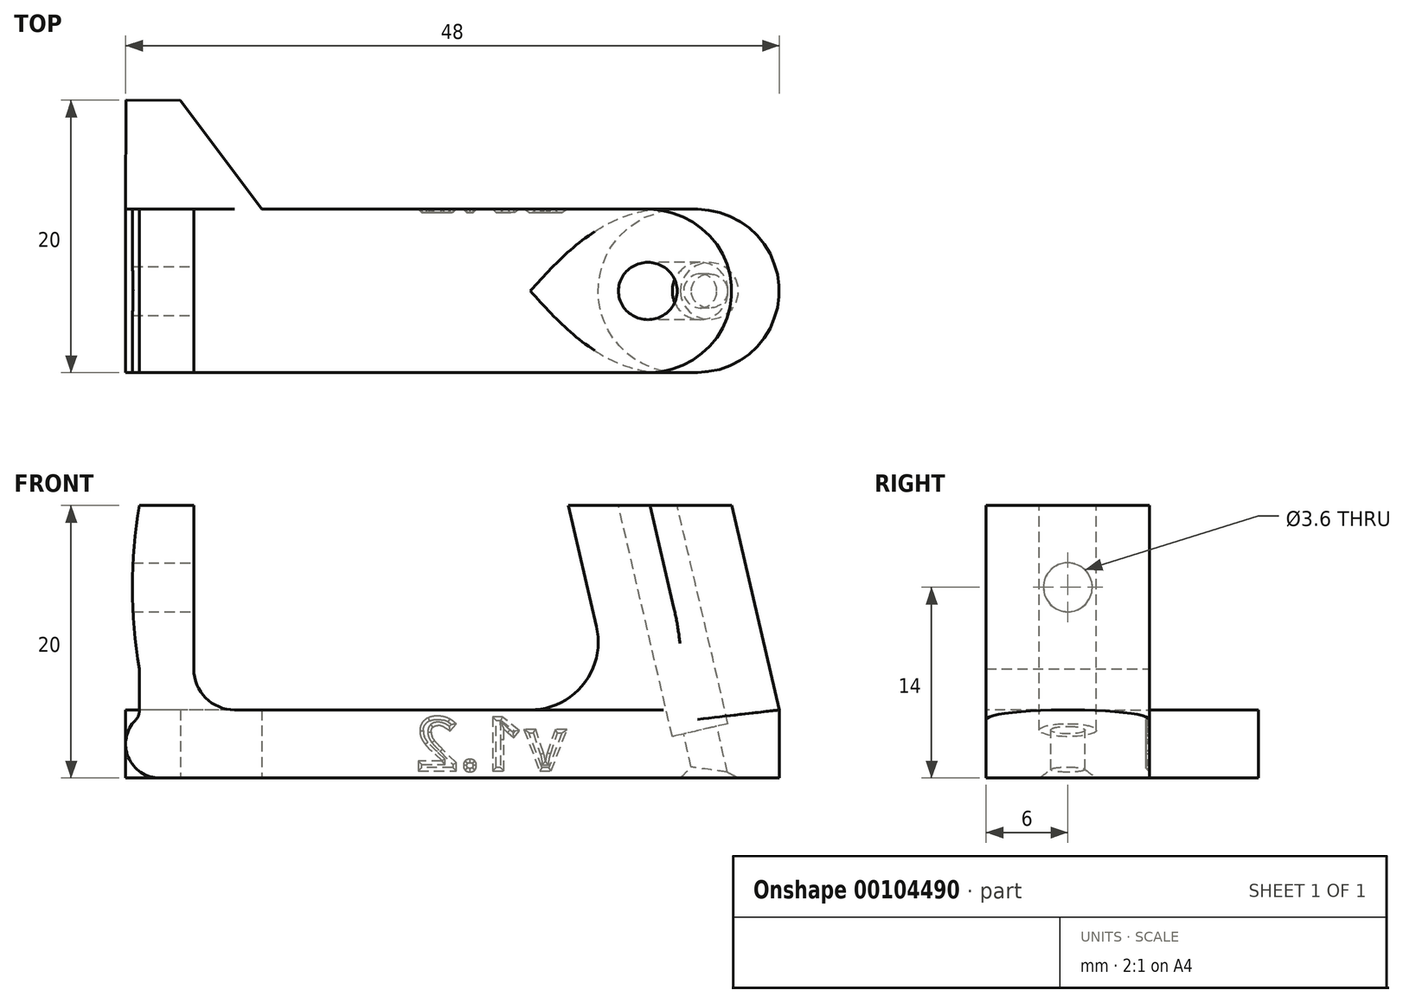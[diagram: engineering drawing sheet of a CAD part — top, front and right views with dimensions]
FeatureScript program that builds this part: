
annotation { "Feature Type Name" : "Feature", "Feature Type Description" : "" }
export const myFeature = defineFeature(function(context is Context, id is Id, definition is map)
    precondition{}
    {
        {
            var Q0;
            Q0=qCreatedBy(makeId("Front.planeOp"),FACE);
            var sketch = newSketch(context, id + "F0", { "sketchPlane" : qUnion([Q0])});
            skLineSegment(sketch, "E0", {"start": v(-24, 0) * mm, "end": v(24, 0) * mm});
            skLineSegment(sketch, "E1", {"start": v(-24, 0) * mm, "end": v(-24, 20) * mm, "construction": true});
            skLineSegment(sketch, "E2", {"start": v(-24, 20) * mm, "end": v(-19, 20) * mm});
            skLineSegment(sketch, "E3", {"start": v(24, 20) * mm, "end": v(20.5, 20) * mm, "construction": true});
            skLineSegment(sketch, "E4", {"start": v(-19, 20) * mm, "end": v(-19, 8) * mm});
            skLineSegment(sketch, "E5", {"start": v(20.5, 20) * mm, "end": v(8.5, 20) * mm, "construction": true});
            skLineSegment(sketch, "E6", {"start": v(24, 0) * mm, "end": v(24, 5) * mm});
            skLineSegment(sketch, "E7", {"start": v(24, 5) * mm, "end": v(24, 20) * mm, "construction": true});
            skLineSegment(sketch, "E8", {"start": v(20.5, 20) * mm, "end": v(24, 5) * mm});
            skLineSegment(sketch, "E9", {"start": v(5.7, 5) * mm, "end": v(-16, 5) * mm});
            skLineSegment(sketch, "E10", {"start": v(-24, 20) * mm, "end": v(-23, 20) * mm});
            skLineSegment(sketch, "E11", {"start": v(8.5, 20) * mm, "end": v(10.57, 11.14) * mm});
            skPoint(sketch, "E12.end.orphan", {"position": v(-23, 0) * mm});
            skLineSegment(sketch, "E13", {"start": v(-23, 20) * mm, "end": v(-23, 14) * mm, "construction": true});
            skLineSegment(sketch, "E14", {"start": v(-23, 14) * mm, "end": v(-23, 8) * mm, "construction": true});
            skLineSegment(sketch, "E15", {"start": v(-23, 5) * mm, "end": v(-23, 8) * mm});
            skArc(sketch, "E16", {"start": v(-23, 5) * mm, "mid": v(-24, 2.5) * mm, "end": v(-23, 0) * mm, "construction": true});
            skLineSegment(sketch, "E17", {"start": v(-23, 8) * mm, "end": v(-24, 8) * mm});
            skArc(sketch, "E18", {"start": v(-23, 20) * mm, "mid": v(-23.5, 14) * mm, "end": v(-23, 8) * mm});
            skPoint(sketch, "E19.visualSharp", {"position": v(-19, 5) * mm});
            skArc(sketch, "E19.filletArc", {"start": v(-19, 8) * mm, "mid": v(-18.12, 5.88) * mm, "end": v(-16, 5) * mm});
            skLineSegment(sketch, "E20", {"start": v(8.5, 20) * mm, "end": v(19.88, 22.66) * mm});
            skLineSegment(sketch, "E21", {"start": v(19.88, 22.66) * mm, "end": v(20.5, 20) * mm});
            skLineSegment(sketch, "E22", {"start": v(10.57, 11.14) * mm, "end": v(10.57, 11.14) * mm});
            skLineSegment(sketch, "E23", {"start": v(5.7, 5) * mm, "end": v(5.7, 5) * mm});
            skPoint(sketch, "E24.visualSharp", {"position": v(12, 5) * mm});
            skArc(sketch, "E24.filletArc", {"start": v(5.7, 5) * mm, "mid": v(9.62, 6.9) * mm, "end": v(10.57, 11.14) * mm});
            skLineSegment(sketch, "E25", {"start": v(-23.5, 20) * mm, "end": v(-23.5, 8) * mm, "construction": true});
            skArc(sketch, "E26", {"start": v(-23.29, 4.25) * mm, "mid": v(-23.8, 1.53) * mm, "end": v(-21.5, 0) * mm});
            skLineSegment(sketch, "E27", {"start": v(-23, 5) * mm, "end": v(-23, 4.97) * mm});
            skPoint(sketch, "E28.visualSharp", {"position": v(-23, 4.5) * mm});
            skArc(sketch, "E28.filletArc", {"start": v(-23.29, 4.25) * mm, "mid": v(-23.07, 4.58) * mm, "end": v(-23, 4.97) * mm});
            skSolve(sketch);
        }
        {
            var Q0;
            Q0 = qSketchRegion(id + "F0", true);
            extrude(context, id + "F1", {"entities" : qUnion([Q0]), "depth" : 12 * mm});
        }
        {
            var Q0;
            Q0=makeQuery(id+"F1.opExtrude","CAP_EDGE",EDGE,{"disambiguationData":[OSD([sQuery(id+"F0.wireOp",EDGE,"E8"),sQuery(id+"F0.wireOp",EDGE,"E21")])],"isStart":false});
            var Q1;
            Q1=makeQuery(id+"F1.opExtrude","CAP_EDGE",EDGE,{"disambiguationData":[OSD([sQuery(id+"F0.wireOp",EDGE,"E8"),sQuery(id+"F0.wireOp",EDGE,"E21")])],"isStart":true});
            var Q2;
            Q2=makeQuery(id+"F1.opExtrude","CAP_EDGE",EDGE,{"disambiguationData":[OSD([sQuery(id+"F0.wireOp",EDGE,"E6")])],"isStart":false});
            var Q3;
            Q3=makeQuery(id+"F1.opExtrude","CAP_EDGE",EDGE,{"disambiguationData":[OSD([sQuery(id+"F0.wireOp",EDGE,"E6")])],"isStart":true});
            var Q4;
            Q4=makeQuery(id+"F1.opExtrude","CAP_EDGE",EDGE,{"disambiguationData":[OSD([sQuery(id+"F0.wireOp",EDGE,"E11")])],"isStart":false});
            var Q5;
            Q5=makeQuery(id+"F1.opExtrude","CAP_EDGE",EDGE,{"disambiguationData":[OSD([sQuery(id+"F0.wireOp",EDGE,"E11")])],"isStart":true});
            var Q6;
            Q6=makeQuery(id+"F1.opExtrude","CAP_EDGE",EDGE,{"disambiguationData":[OSD([sQuery(id+"F0.wireOp",EDGE,"E24.filletArc")])],"isStart":false});
            var Q7;
            Q7=makeQuery(id+"F1.opExtrude","CAP_EDGE",EDGE,{"disambiguationData":[OSD([sQuery(id+"F0.wireOp",EDGE,"E24.filletArc")])],"isStart":true});
            fillet(context, id + "F2", {"entities" : qUnion([Q0, Q1, Q2, Q3, Q4, Q5, Q6, Q7]), "radius" : 6 * mm, "allowEdgeOverflow" : false});
        }
        {
            var Q0;
            Q0=qCreatedBy(makeId("Right.planeOp"),FACE);
            var sketch = newSketch(context, id + "F3", { "sketchPlane" : qUnion([Q0])});
            skLineSegment(sketch, "E29.0", {"start": v(-12, 5) * mm, "end": v(0, 5) * mm});
            skLineSegment(sketch, "E30.0.3", {"start": v(0, 0) * mm, "end": v(-12, 0) * mm});
            skLineSegment(sketch, "E30.0.7", {"start": v(-12, 0) * mm, "end": v(0, 0) * mm});
            skLineSegment(sketch, "E31", {"start": v(-12, 5) * mm, "end": v(-12, 0) * mm});
            skLineSegment(sketch, "E32", {"start": v(0, 0) * mm, "end": v(0, 5) * mm});
            skSolve(sketch);
        }
        {
            var Q0;
            Q0 = qSketchRegion(id + "F3", true);
            var Q1;
            Q1=makeQuery(id+"F2.opFillet","SPLIT",FACE,{"disambiguationData":[OD(1.0)],"derivedFrom":makeQuery(id+"F1.opExtrude","CAP_FACE",FACE,{"disambiguationData":[OSD([sQuery(id+"F0.wireOp",EDGE,"E0"),sQuery(id+"F0.wireOp",EDGE,"E2"),sQuery(id+"F0.wireOp",EDGE,"E4"),sQuery(id+"F0.wireOp",EDGE,"E6"),sQuery(id+"F0.wireOp",EDGE,"E8"),sQuery(id+"F0.wireOp",EDGE,"E9"),sQuery(id+"F0.wireOp",EDGE,"E11"),sQuery(id+"F0.wireOp",EDGE,"E15"),sQuery(id+"F0.wireOp",EDGE,"E16"),sQuery(id+"F0.wireOp",EDGE,"E18"),sQuery(id+"F0.wireOp",EDGE,"E19.filletArc"),sQuery(id+"F0.wireOp",EDGE,"E20"),sQuery(id+"F0.wireOp",EDGE,"E21"),sQuery(id+"F0.wireOp",EDGE,"E24.filletArc")])],"isStart":false})});
            extrude(context, id + "F4", {"entities" : qUnion([Q0]), "operationType" : NewBodyOperationType.ADD, "endBoundEntityFace" : qUnion([Q1]), "depth" : 13.1 * mm, "hasSecondDirection" : true, "secondDirectionOppositeDirection" : true, "secondDirectionDepth" : 10 * mm});
        }
        {
            var Q0;
            {var subQ0=sQuery(id+"F3.wireOp",EDGE,"E29.0");var subQ3=sQuery(id+"F3.wireOp",EDGE,"E32");Q0=makeQuery(id+"F4.boolean.opBoolean","SPLIT",FACE,{"disambiguationData":[TD([makeQuery(id+"F4.opExtrude","SWEPT_FACE",FACE,{"disambiguationData":[OSD([subQ3])]})])],"derivedFrom":makeQuery(id+"F4.opExtrude","CAP_FACE",FACE,{"disambiguationData":[OSD([subQ0,sQuery(id+"F3.wireOp",EDGE,"E30.0.7"),sQuery(id+"F3.wireOp",EDGE,"E31"),subQ3])],"isStart":false})});}
            var sketch = newSketch(context, id + "F5", { "sketchPlane" : qUnion([Q0])});
            skLineSegment(sketch, "E33.bottom", {"start": v(0, 5) * mm, "end": v(-12, 5) * mm});
            skLineSegment(sketch, "E33.top", {"start": v(0, 0) * mm, "end": v(-12, 0) * mm});
            skLineSegment(sketch, "E33.left", {"start": v(0, 5) * mm, "end": v(0, 0) * mm});
            skLineSegment(sketch, "E33.right", {"start": v(-12, 5) * mm, "end": v(-12, 0) * mm});
            skLineSegment(sketch, "E34.0", {"start": v(-12, 5) * mm, "end": v(-12, 1.86) * mm});
            skSolve(sketch);
        }
        {
            var Q0;
            Q0 = qSketchRegion(id + "F5", true);
            extrude(context, id + "F6", {"entities" : qUnion([Q0]), "operationType" : NewBodyOperationType.ADD, "depth" : 2.72 * mm});
        }
        {
            var Q0;
            Q0=makeQuery(id+"F1.opExtrude","SWEPT_FACE",FACE,{"disambiguationData":[OSD([sQuery(id+"F0.wireOp",EDGE,"E20")])]});
            var sketch = newSketch(context, id + "F7", { "sketchPlane" : qUnion([Q0])});
            skCircle(sketch, "E35", {"center": v(18.5, -6) * mm, "radius": 2.1 * mm});
            skSolve(sketch);
        }
        {
            var Q0;
            Q0 = qSketchRegion(id + "F7", true);
            extrude(context, id + "F8", {"entities" : qUnion([Q0]), "operationType" : NewBodyOperationType.REMOVE, "oppositeDirection" : true, "depth" : 18.25 * mm});
        }
        {
            var Q0;
            Q0=makeQuery(id+"F8.boolean.opBoolean","COPY",FACE,{"derivedFrom":makeQuery(id+"F8.opExtrude","CAP_FACE",FACE,{"disambiguationData":[OSD([sQuery(id+"F7.wireOp",EDGE,"E35")])],"isStart":false})});
            var sketch = newSketch(context, id + "F9", { "sketchPlane" : qUnion([Q0])});
            skCircle(sketch, "E36", {"center": v(18.5, -6) * mm, "radius": 1.25 * mm});
            skSolve(sketch);
        }
        {
            var Q0;
            Q0 = qSketchRegion(id + "F9", true);
            extrude(context, id + "F10", {"entities" : qUnion([Q0]), "operationType" : NewBodyOperationType.REMOVE, "oppositeDirection" : true, "depth" : 25 * mm});
        }
        {
            var Q0;
            Q0=makeQuery(id+"F10.boolean.opBoolean","INTERSECT",EDGE,{"derivedFrom":[makeQuery(id+"F4.boolean.opBoolean","MERGE",FACE,{"derivedFrom":[makeQuery(id+"F1.opExtrude","SWEPT_FACE",FACE,{"disambiguationData":[OSD([sQuery(id+"F0.wireOp",EDGE,"E0")])]}),makeQuery(id+"F4.opExtrude","SWEPT_FACE",FACE,{"disambiguationData":[OSD([sQuery(id+"F3.wireOp",EDGE,"E30.0.7")])]})]}),makeQuery(id+"F10.opExtrude","SWEPT_FACE",FACE,{"disambiguationData":[OSD([sQuery(id+"F9.wireOp",EDGE,"E36")])]})]});
            chamfer(context, id + "F11", {"entities" : qUnion([Q0]), "chamferType" : ChamferType.OFFSET_ANGLE, "width" : 1 * mm, "oppositeDirection" : false, "angle" : 45 * degree, "tangentPropagation" : true});
        }
        {
            var Q0;
            Q0=makeQuery(id+"F1.opExtrude","SWEPT_FACE",FACE,{"disambiguationData":[OSD([sQuery(id+"F0.wireOp",EDGE,"E4")])]});
            var sketch = newSketch(context, id + "F12", { "sketchPlane" : qUnion([Q0])});
            skLineSegment(sketch, "E37", {"start": v(-6, 20) * mm, "end": v(-6, 14) * mm});
            skCircle(sketch, "E38", {"center": v(-6, 14) * mm, "radius": 1.8 * mm});
            skSolve(sketch);
        }
        {
            var Q0;
            Q0 = qSketchRegion(id + "F12", true);
            extrude(context, id + "F13", {"entities" : qUnion([Q0]), "operationType" : NewBodyOperationType.REMOVE, "oppositeDirection" : true, "depth" : 25 * mm});
        }
        {
            var Q0;
            Q0=qCreatedBy(makeId("Right.planeOp"),FACE);
            var sketch = newSketch(context, id + "F14", { "sketchPlane" : qUnion([Q0])});
            skLineSegment(sketch, "E39.0", {"start": v(-12, 20) * mm, "end": v(0, 20) * mm});
            skLineSegment(sketch, "E40.top", {"start": v(-12, 36.1) * mm, "end": v(0, 36.1) * mm});
            skLineSegment(sketch, "E40.left", {"start": v(-12, 20) * mm, "end": v(-12, 36.1) * mm});
            skLineSegment(sketch, "E40.right", {"start": v(0, 20) * mm, "end": v(0, 36.1) * mm});
            skSolve(sketch);
        }
        {
            var Q0;
            Q0 = qSketchRegion(id + "F14", true);
            extrude(context, id + "F15", {"entities" : qUnion([Q0]), "operationType" : NewBodyOperationType.REMOVE, "depth" : 25 * mm});
        }
        {
            var Q0;
            {var subQ0=makeQuery(id+"F1.opExtrude","CAP_FACE",FACE,{"disambiguationData":[OSD([sQuery(id+"F0.wireOp",EDGE,"E0"),sQuery(id+"F0.wireOp",EDGE,"E2"),sQuery(id+"F0.wireOp",EDGE,"E4"),sQuery(id+"F0.wireOp",EDGE,"E6"),sQuery(id+"F0.wireOp",EDGE,"E8"),sQuery(id+"F0.wireOp",EDGE,"E9"),sQuery(id+"F0.wireOp",EDGE,"E11"),sQuery(id+"F0.wireOp",EDGE,"E15"),sQuery(id+"F0.wireOp",EDGE,"E16"),sQuery(id+"F0.wireOp",EDGE,"E18"),sQuery(id+"F0.wireOp",EDGE,"E19.filletArc"),sQuery(id+"F0.wireOp",EDGE,"E20"),sQuery(id+"F0.wireOp",EDGE,"E21"),sQuery(id+"F0.wireOp",EDGE,"E24.filletArc")])],"isStart":true});Q0=makeQuery(id+"F6.boolean.opBoolean","MERGE",FACE,{"derivedFrom":[makeQuery(id+"F4.boolean.opBoolean","MERGE",FACE,{"derivedFrom":[makeQuery(id+"F2.opFillet","SPLIT",FACE,{"disambiguationData":[OD(0.0)],"derivedFrom":subQ0}),makeQuery(id+"F2.opFillet","SPLIT",FACE,{"disambiguationData":[OD(1.0)],"derivedFrom":subQ0}),makeQuery(id+"F4.opExtrude","SWEPT_FACE",FACE,{"disambiguationData":[OSD([sQuery(id+"F3.wireOp",EDGE,"E32")])]})]}),makeQuery(id+"F6.opExtrude","SWEPT_FACE",FACE,{"disambiguationData":[OSD([sQuery(id+"F5.wireOp",EDGE,"E33.left")])]})]});}
            var sketch = newSketch(context, id + "F16", { "sketchPlane" : qUnion([Q0])});
            skText(sketch, "E41", { "text": "v1.2", "fontName": "OpenSans-Bold.ttf"});
            const initialGuessF16  = {"E41": [-0.0084, 0.00053, 1, 0, 0.004]};
            skSetInitialGuess(sketch, initialGuessF16);
            skSolve(sketch);
        }
        {
            var Q0;
            Q0 = qSketchRegion(id + "F16", true);
            extrude(context, id + "F17", {"entities" : qUnion([Q0]), "operationType" : NewBodyOperationType.REMOVE, "oppositeDirection" : true, "depth" : .25 * mm});
        }
        {
            var Q0;
            Q0=makeQuery(id+"F17.boolean.opBoolean","COPY",FACE,{"derivedFrom":makeQuery(id+"F17.opExtrude","CAP_FACE",FACE,{"disambiguationData":[OSD([sQuery(id+"F16.wireOp",EDGE,"E41.sketch_text.stroke-10"),sQuery(id+"F16.wireOp",EDGE,"E41.sketch_text.stroke-11"),sQuery(id+"F16.wireOp",EDGE,"E41.sketch_text.stroke-12"),sQuery(id+"F16.wireOp",EDGE,"E41.sketch_text.stroke-13"),sQuery(id+"F16.wireOp",EDGE,"E41.sketch_text.stroke-14"),sQuery(id+"F16.wireOp",EDGE,"E41.sketch_text.stroke-15"),sQuery(id+"F16.wireOp",EDGE,"E41.sketch_text.stroke-16"),sQuery(id+"F16.wireOp",EDGE,"E41.sketch_text.stroke-17"),sQuery(id+"F16.wireOp",EDGE,"E41.sketch_text.stroke-18"),sQuery(id+"F16.wireOp",EDGE,"E41.sketch_text.stroke-19")])],"isStart":false})});
            var Q1;
            Q1=makeQuery(id+"F17.boolean.opBoolean","COPY",FACE,{"derivedFrom":makeQuery(id+"F17.opExtrude","CAP_FACE",FACE,{"disambiguationData":[OSD([sQuery(id+"F16.wireOp",EDGE,"E41.sketch_text.stroke-28"),sQuery(id+"F16.wireOp",EDGE,"E41.sketch_text.stroke-29"),sQuery(id+"F16.wireOp",EDGE,"E41.sketch_text.stroke-30"),sQuery(id+"F16.wireOp",EDGE,"E41.sketch_text.stroke-31"),sQuery(id+"F16.wireOp",EDGE,"E41.sketch_text.stroke-32"),sQuery(id+"F16.wireOp",EDGE,"E41.sketch_text.stroke-33"),sQuery(id+"F16.wireOp",EDGE,"E41.sketch_text.stroke-34"),sQuery(id+"F16.wireOp",EDGE,"E41.sketch_text.stroke-35"),sQuery(id+"F16.wireOp",EDGE,"E41.sketch_text.stroke-36"),sQuery(id+"F16.wireOp",EDGE,"E41.sketch_text.stroke-37")])],"isStart":false})});
            var Q2;
            Q2=makeQuery(id+"F17.boolean.opBoolean","COPY",FACE,{"derivedFrom":makeQuery(id+"F17.opExtrude","CAP_FACE",FACE,{"disambiguationData":[OSD([sQuery(id+"F16.wireOp",EDGE,"E41.sketch_text.stroke-20"),sQuery(id+"F16.wireOp",EDGE,"E41.sketch_text.stroke-21"),sQuery(id+"F16.wireOp",EDGE,"E41.sketch_text.stroke-22"),sQuery(id+"F16.wireOp",EDGE,"E41.sketch_text.stroke-23"),sQuery(id+"F16.wireOp",EDGE,"E41.sketch_text.stroke-24"),sQuery(id+"F16.wireOp",EDGE,"E41.sketch_text.stroke-25"),sQuery(id+"F16.wireOp",EDGE,"E41.sketch_text.stroke-26"),sQuery(id+"F16.wireOp",EDGE,"E41.sketch_text.stroke-27")])],"isStart":false})});
            var Q3;
            Q3=makeQuery(id+"F17.boolean.opBoolean","COPY",FACE,{"derivedFrom":makeQuery(id+"F17.opExtrude","CAP_FACE",FACE,{"disambiguationData":[OSD([sQuery(id+"F16.wireOp",EDGE,"E41.sketch_text.stroke-0"),sQuery(id+"F16.wireOp",EDGE,"E41.sketch_text.stroke-1"),sQuery(id+"F16.wireOp",EDGE,"E41.sketch_text.stroke-2"),sQuery(id+"F16.wireOp",EDGE,"E41.sketch_text.stroke-3"),sQuery(id+"F16.wireOp",EDGE,"E41.sketch_text.stroke-4"),sQuery(id+"F16.wireOp",EDGE,"E41.sketch_text.stroke-5"),sQuery(id+"F16.wireOp",EDGE,"E41.sketch_text.stroke-6"),sQuery(id+"F16.wireOp",EDGE,"E41.sketch_text.stroke-7"),sQuery(id+"F16.wireOp",EDGE,"E41.sketch_text.stroke-8"),sQuery(id+"F16.wireOp",EDGE,"E41.sketch_text.stroke-9")])],"isStart":false})});
            chamfer(context, id + "F18", {"entities" : qUnion([Q0, Q1, Q2, Q3]), "width" : .25 * mm, "tangentPropagation" : true});
        }
        {
            var Q0;
            Q0=makeQuery(id+"F4.boolean.opBoolean","MERGE",FACE,{"derivedFrom":[makeQuery(id+"F1.opExtrude","SWEPT_FACE",FACE,{"disambiguationData":[OSD([sQuery(id+"F0.wireOp",EDGE,"E0")])]}),makeQuery(id+"F4.opExtrude","SWEPT_FACE",FACE,{"disambiguationData":[OSD([sQuery(id+"F3.wireOp",EDGE,"E30.0.7")])]})]});
            var sketch = newSketch(context, id + "F20", { "sketchPlane" : qUnion([Q0])});
            skPoint(sketch, "E42.0.end.orphan", {"position": v(-23, 0) * mm});
            skPoint(sketch, "E42.0.start.orphan", {"position": v(-24, 0) * mm});
            skLineSegment(sketch, "E43", {"start": v(-24, 0) * mm, "end": v(-14, 0) * mm});
            skLineSegment(sketch, "E44", {"start": v(-14, 0) * mm, "end": v(-14, -8) * mm});
            skLineSegment(sketch, "E45", {"start": v(-24, 0) * mm, "end": v(-24, -8) * mm});
            skLineSegment(sketch, "E46", {"start": v(-24, -8) * mm, "end": v(-20, -8) * mm});
            skLineSegment(sketch, "E47", {"start": v(-20, -8) * mm, "end": v(-14, 0) * mm});
            skSolve(sketch);
        }
        {
            var Q0;
            Q0 = qSketchRegion(id + "F20", true);
            var Q1;
            Q1=makeQuery(id+"F6.boolean.opBoolean","MERGE",FACE,{"derivedFrom":[makeQuery(id+"F4.boolean.opBoolean","MERGE",FACE,{"derivedFrom":[makeQuery(id+"F1.opExtrude","SWEPT_FACE",FACE,{"disambiguationData":[OSD([sQuery(id+"F0.wireOp",EDGE,"E9")])]}),makeQuery(id+"F4.opExtrude","SWEPT_FACE",FACE,{"disambiguationData":[OSD([sQuery(id+"F3.wireOp",EDGE,"E29.0")])]})]}),makeQuery(id+"F6.opExtrude","SWEPT_FACE",FACE,{"disambiguationData":[OSD([sQuery(id+"F5.wireOp",EDGE,"E33.bottom")])]})]});
            extrude(context, id + "F21", {"entities" : qUnion([Q0]), "operationType" : NewBodyOperationType.ADD, "endBound" : BoundingType.UP_TO_SURFACE, "oppositeDirection" : true, "endBoundEntityFace" : qUnion([Q1]), "depth" : 25 * mm});
        }
    });
